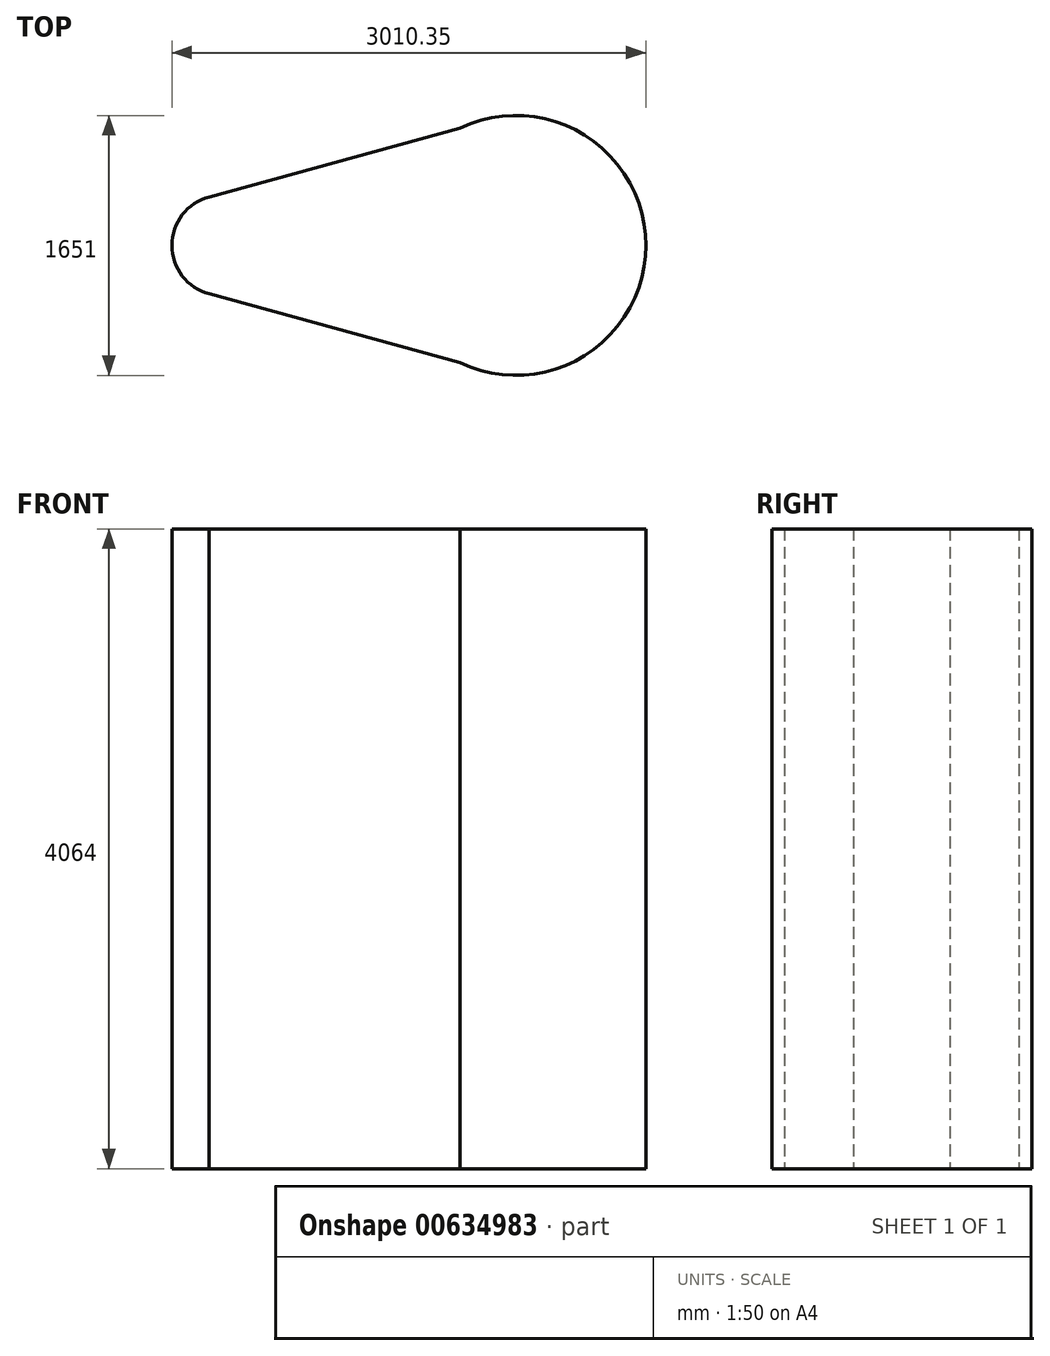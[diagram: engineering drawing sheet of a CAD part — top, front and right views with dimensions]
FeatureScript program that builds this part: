
annotation { "Feature Type Name" : "Feature", "Feature Type Description" : "" }
export const myFeature = defineFeature(function(context is Context, id is Id, definition is map)
    precondition{}
    {
        {
            var Q0;
            Q0=qCreatedBy(makeId("Top.planeOp"),FACE);
            var sketch = newSketch(context, id + "F0", { "sketchPlane" : qUnion([Q0])});
            skCircle(sketch, "E0", {"center": v(-1512.25, 0) * mm, "radius": 317.5 * mm});
            skCircle(sketch, "E1", {"center": v(355.1, 0) * mm, "radius": 825.5 * mm});
            skLineSegment(sketch, "E2", {"start": v(-1591.88, 307.35) * mm, "end": v(0, 745.22) * mm});
            skLineSegment(sketch, "E3", {"start": v(-1591.88, -307.35) * mm, "end": v(0, -745.22) * mm});
            skSolve(sketch);
        }
        {
            var Q0;
            Q0 = qSketchRegion(id + "F0", true);
            extrude(context, id + "F1", {"entities" : qUnion([Q0]), "depth" : 4064 * mm, "offsetDistance" : 25.4 * mm});
        }
    });
